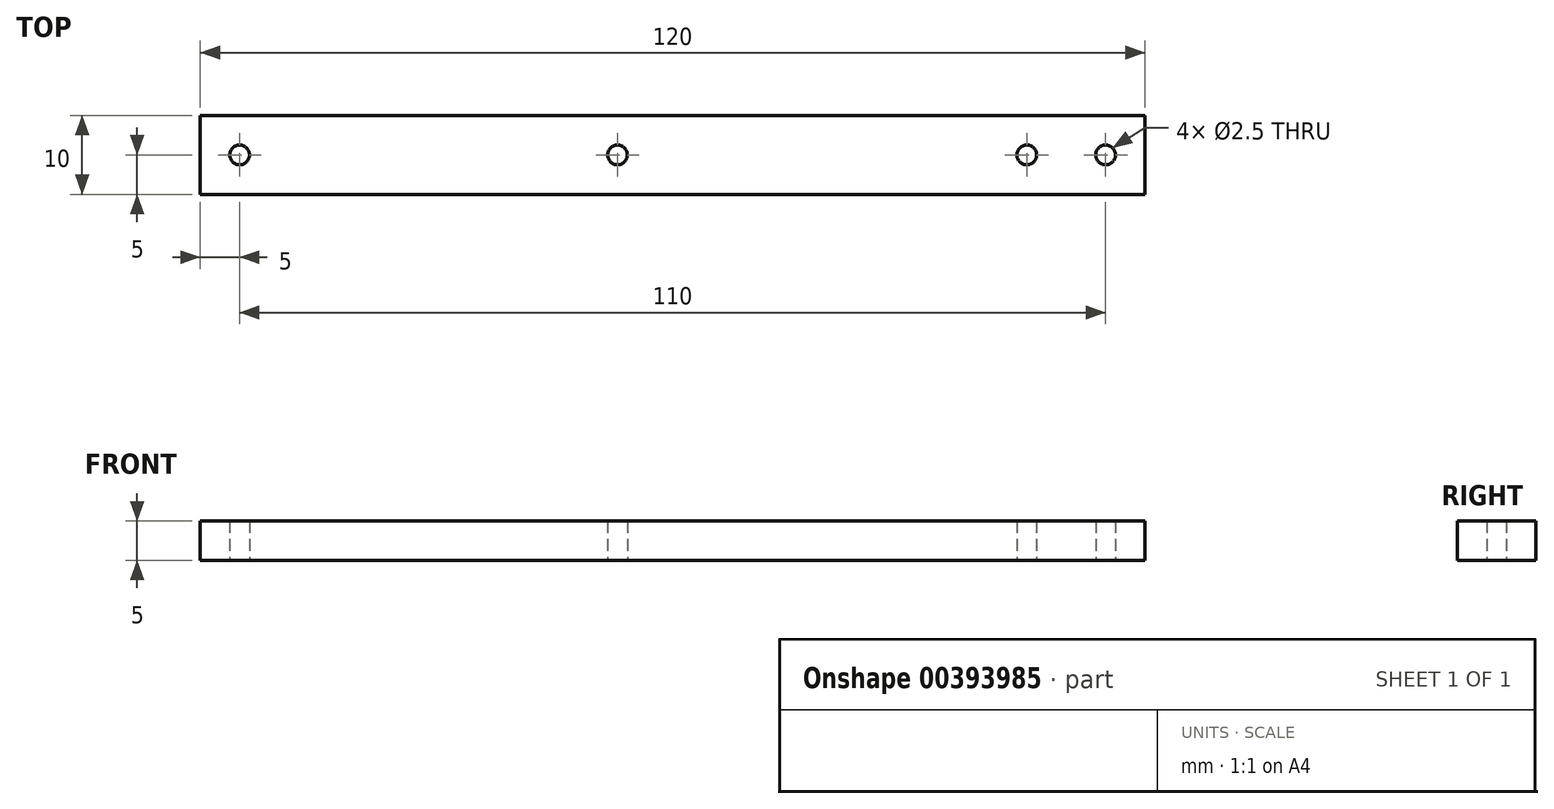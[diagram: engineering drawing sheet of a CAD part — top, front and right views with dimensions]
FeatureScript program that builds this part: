
annotation { "Feature Type Name" : "Feature", "Feature Type Description" : "" }
export const myFeature = defineFeature(function(context is Context, id is Id, definition is map)
    precondition{}
    {
        {
            var Q0;
            Q0=qCreatedBy(makeId("Top.planeOp"),FACE);
            var sketch = newSketch(context, id + "F0", { "sketchPlane" : qUnion([Q0])});
            skLineSegment(sketch, "E0.bottom", {"start": v(65, 5) * mm, "end": v(-55, 5) * mm});
            skLineSegment(sketch, "E0.top", {"start": v(65, -5) * mm, "end": v(-55, -5) * mm});
            skLineSegment(sketch, "E0.right", {"start": v(-55, 5) * mm, "end": v(-55, -5) * mm});
            skPoint(sketch, "E0.middle", {"position": v(0, 0) * mm});
            skCircle(sketch, "E1", {"center": v(-50, 0) * mm, "radius": 1.25 * mm});
            skCircle(sketch, "E2", {"center": v(-2, 0) * mm, "radius": 1.25 * mm});
            skLineSegment(sketch, "E3.right", {"start": v(65, 5) * mm, "end": v(65, -5) * mm});
            skCircle(sketch, "E4.MirrorC", {"center": v(50, 0) * mm, "radius": 1.25 * mm});
            skCircle(sketch, "E5", {"center": v(60, 0) * mm, "radius": 1.25 * mm});
            skSolve(sketch);
        }
        {
            var Q0;
            Q0=qSketchRegion(id+"F0",true);
            extrude(context, id + "F1", {"entities" : qUnion([Q0]), "depth" : 5 * mm});
        }
    });
